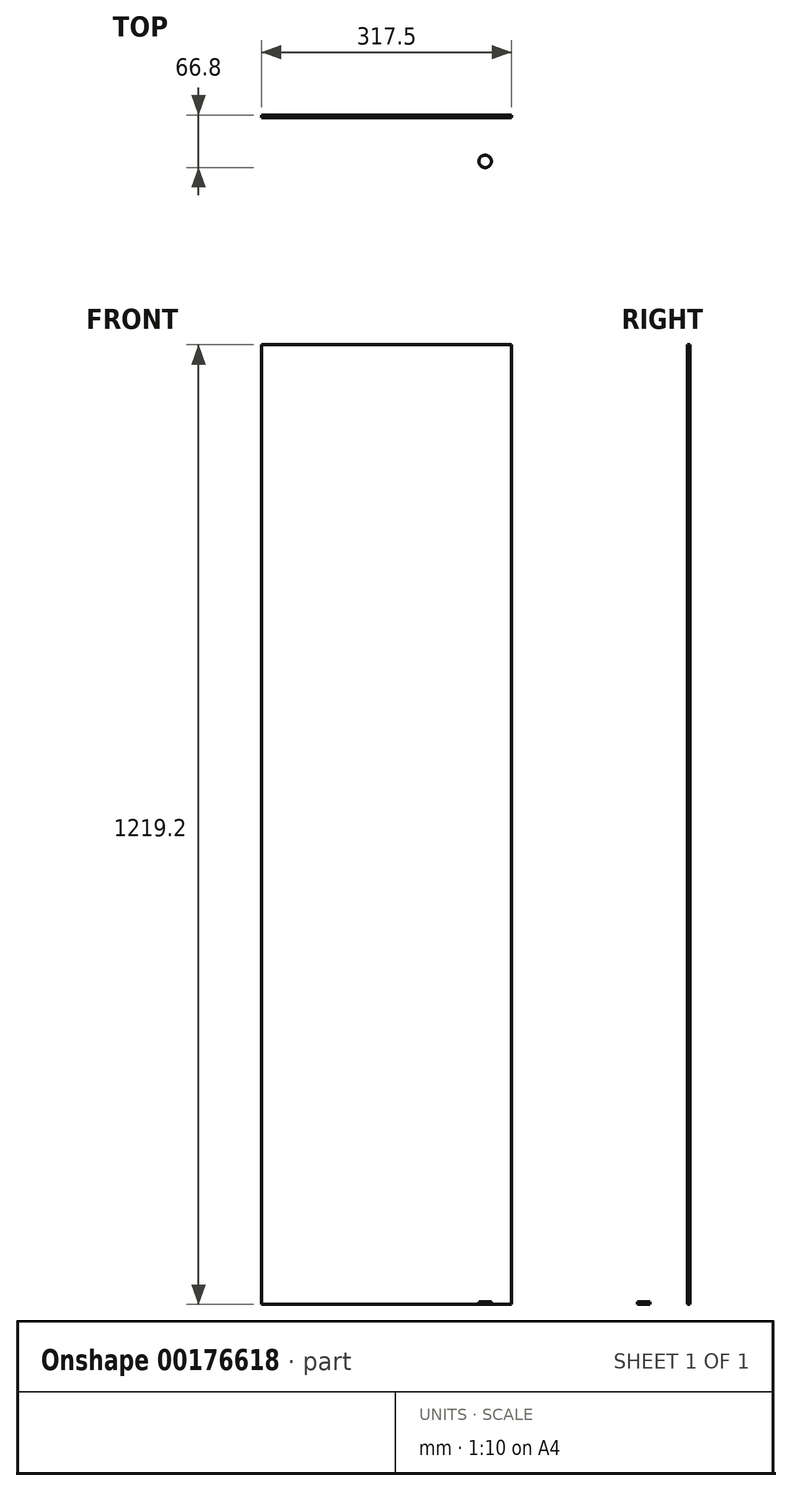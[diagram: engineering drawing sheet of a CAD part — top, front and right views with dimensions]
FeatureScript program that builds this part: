
annotation { "Feature Type Name" : "Feature", "Feature Type Description" : "" }
export const myFeature = defineFeature(function(context is Context, id is Id, definition is map)
    precondition{}
    {
        {
            var Q0;
            Q0=qCreatedBy(makeId("Front.planeOp"),FACE);
            var sketch = newSketch(context, id + "F0", { "sketchPlane" : qUnion([Q0])});
            skLineSegment(sketch, "E0.bottom", {"start": v(158.75, 609.6) * mm, "end": v(-158.75, 609.6) * mm});
            skLineSegment(sketch, "E0.top", {"start": v(158.75, -609.6) * mm, "end": v(-158.75, -609.6) * mm});
            skLineSegment(sketch, "E0.left", {"start": v(158.75, 609.6) * mm, "end": v(158.75, -609.6) * mm});
            skLineSegment(sketch, "E0.right", {"start": v(-158.75, 609.6) * mm, "end": v(-158.75, -609.6) * mm});
            skPoint(sketch, "E0.middle", {"position": v(0, 0) * mm});
            skSolve(sketch);
        }
        {
            var Q0;
            Q0=makeQuery(id+"F0.imprint","IMPRINT",FACE,{"disambiguationData":[TD([[makeQuery(id+"F0.imprint","IMPRINT",EDGE,{"derivedFrom":sQuery(id+"F0.wireOp",EDGE,"E0.bottom")}),1.0]])]});
            extrude(context, id + "F1", {"entities" : qUnion([Q0]), "depth" : 3.42 * mm});
        }
        {
            var Q0;
            Q0=makeQuery(id+"F1.opExtrude","CAP_FACE",FACE,{"disambiguationData":[OSD([sQuery(id+"F0.wireOp",EDGE,"E0.bottom"),sQuery(id+"F0.wireOp",EDGE,"E0.top"),sQuery(id+"F0.wireOp",EDGE,"E0.left"),sQuery(id+"F0.wireOp",EDGE,"E0.right")])],"isStart":false});
            var sketch = newSketch(context, id + "F2", { "sketchPlane" : qUnion([Q0])});
            skLineSegment(sketch, "E1.bottom", {"start": v(-158.75, -609.6) * mm, "end": v(158.75, -609.6) * mm});
            skLineSegment(sketch, "E1.top", {"start": v(-158.75, -606.18) * mm, "end": v(158.75, -606.18) * mm});
            skLineSegment(sketch, "E1.left", {"start": v(-158.75, -609.6) * mm, "end": v(-158.75, -606.18) * mm});
            skLineSegment(sketch, "E1.right", {"start": v(158.75, -609.6) * mm, "end": v(158.75, -606.18) * mm});
            skSolve(sketch);
        }
        {
            var Q0;
            Q0=makeQuery(id+"F2.imprint","IMPRINT",FACE,{"disambiguationData":[TD([[makeQuery(id+"F2.imprint","IMPRINT",EDGE,{"derivedFrom":sQuery(id+"F2.wireOp",EDGE,"E1.bottom")}),-1.0]])]});
            extrude(context, id + "F3", {"entities" : qUnion([Q0]), "operationType" : NewBodyOperationType.ADD, "depth" : 110.88 * mm});
        }
        {
            var Q0;
            Q0=makeQuery(id+"F3.opExtrude","SWEPT_FACE",FACE,{"disambiguationData":[OSD([sQuery(id+"F2.wireOp",EDGE,"E1.top")])]});
            var sketch = newSketch(context, id + "F4", { "sketchPlane" : qUnion([Q0])});
            skLineSegment(sketch, "E2", {"start": v(-158.75, -58.86) * mm, "end": v(158.75, -58.86) * mm, "construction": true});
            skLineSegment(sketch, "E3", {"start": v(0, -3.42) * mm, "end": v(0, -114.3) * mm, "construction": true});
            skCircle(sketch, "E4", {"center": v(-125.41, -58.86) * mm, "radius": 7.94 * mm});
            skCircle(sketch, "E5.MirrorC", {"center": v(125.41, -58.86) * mm, "radius": 7.94 * mm});
            skCircle(sketch, "E6", {"center": v(0, -58.86) * mm, "radius": 7.94 * mm});
            skSolve(sketch);
        }
        {
            var Q0;
            Q0=makeQuery(id+"F4.imprint","IMPRINT",FACE,{"disambiguationData":[TD([[makeQuery(id+"F4.imprint","IMPRINT",EDGE,{"derivedFrom":sQuery(id+"F4.wireOp",EDGE,"E4")}),1.0]])]});
            var Q1;
            Q1=makeQuery(id+"F4.imprint","IMPRINT",FACE,{"disambiguationData":[TD([[makeQuery(id+"F4.imprint","IMPRINT",EDGE,{"derivedFrom":sQuery(id+"F4.wireOp",EDGE,"E6")}),1.0]])]});
            var Q2;
            Q2=makeQuery(id+"F4.imprint","IMPRINT",FACE,{"disambiguationData":[TD([[makeQuery(id+"F4.imprint","IMPRINT",EDGE,{"derivedFrom":sQuery(id+"F4.wireOp",EDGE,"E5.MirrorC")}),-1.0]])]});
            extrude(context, id + "F5", {"entities" : qUnion([Q0, Q1, Q2]), "operationType" : NewBodyOperationType.REMOVE, "endBound" : BoundingType.THROUGH_ALL, "oppositeDirection" : true, "depth" : 25.4 * mm});
        }
    });
